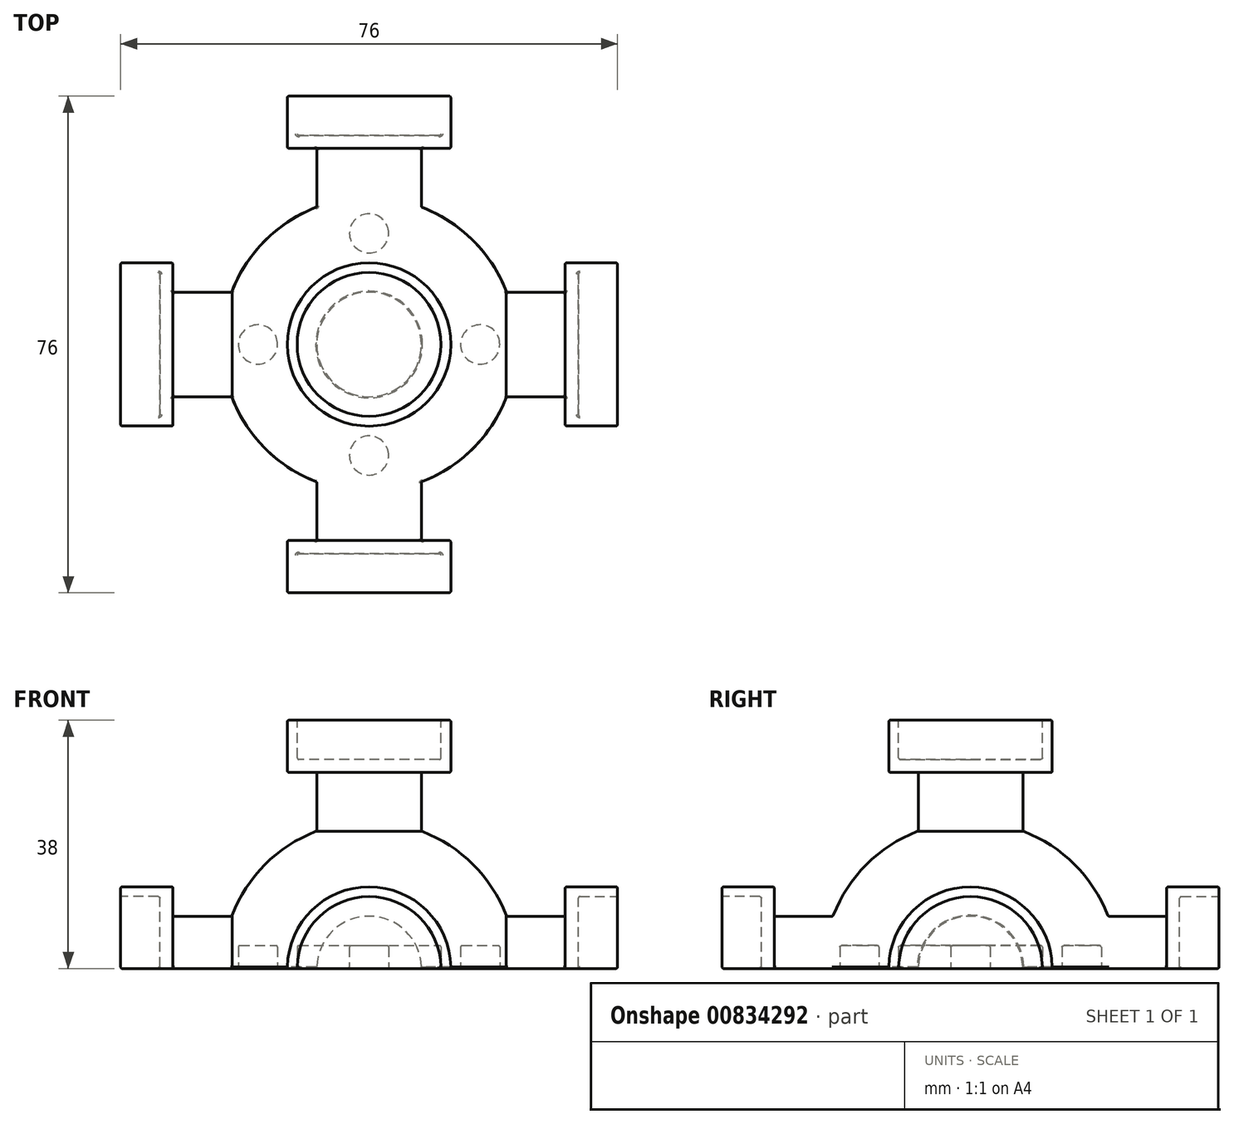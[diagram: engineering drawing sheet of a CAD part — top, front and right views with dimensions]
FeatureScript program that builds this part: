
annotation { "Feature Type Name" : "Feature", "Feature Type Description" : "" }
export const myFeature = defineFeature(function(context is Context, id is Id, definition is map)
    precondition{}
    {
        {
            var Q0;
            Q0=qCreatedBy(makeId("Top.planeOp"),FACE);
            var sketch = newSketch(context, id + "F0", { "sketchPlane" : qUnion([Q0])});
            skCircle(sketch, "E0", {"center": v(0, 0) * mm, "radius": 22.5 * mm});
            skLineSegment(sketch, "E1", {"start": v(0, 22.5) * mm, "end": v(0, -22.5) * mm});
            skSolve(sketch);
        }
        {
            var Q0;
            {var subQ0=sQuery(id+"F0.wireOp",EDGE,"E1");Q0=makeQuery(id+"F0.imprint","IMPRINT",FACE,{"disambiguationData":[TD([[makeQuery(id+"F0.imprint","IMPRINT",EDGE,{"derivedFrom":subQ0}),1.0]])]});}
            var Q1;
            Q1=sQuery(id+"F0.wireOp",EDGE,"E1");
            revolve(context, id + "F1", {"surfaceOperationType" : NewSurfaceOperationType.NEW, "entities" : qUnion([Q0]), "axis" : qUnion([Q1]), "revolveType" : RevolveType.ONE_DIRECTION, "angle" : 180 * degree});
        }
        {
            var Q0;
            Q0=makeQuery(id+"F1.opRevolve","CAP_FACE",FACE,{"disambiguationData":[OSD([sQuery(id+"F0.wireOp",EDGE,"E0"),sQuery(id+"F0.wireOp",EDGE,"E1")])],"isStart":true});
            var sketch = newSketch(context, id + "F2", { "sketchPlane" : qUnion([Q0])});
            skCircle(sketch, "E2", {"center": v(0, 0) * mm, "radius": 11 * mm});
            skCircle(sketch, "E3", {"center": v(0, -17) * mm, "radius": 3 * mm});
            skCircle(sketch, "E4", {"center": v(-17, 0) * mm, "radius": 3 * mm});
            skCircle(sketch, "E5.MirrorC", {"center": v(17, 0) * mm, "radius": 3 * mm});
            skCircle(sketch, "E6.MirrorC", {"center": v(0, 17) * mm, "radius": 3 * mm});
            skSolve(sketch);
        }
        {
            var Q0;
            Q0 = qSketchRegion(id + "F2", true);
            extrude(context, id + "F3", {"entities" : qUnion([Q0]), "operationType" : NewBodyOperationType.REMOVE, "oppositeDirection" : true, "depth" : 3.5 * mm, "offsetDistance" : 25 * mm});
        }
        {
            var Q0;
            Q0=qCreatedBy(makeId("Top.planeOp"),FACE);
            cPlane(context, id + "F4", {"entities" : qUnion([Q0]), "cplaneType" : CPlaneType.OFFSET, "offset" : 20 * mm, "width" : 150 * mm, "height" : 150 * mm});
        }
        {
            var Q0;
            Q0=qCreatedBy(id+"F4.planeOp",FACE);
            var sketch = newSketch(context, id + "F5", { "sketchPlane" : qUnion([Q0])});
            skCircle(sketch, "E7", {"center": v(0, 0) * mm, "radius": 8 * mm});
            skSolve(sketch);
        }
        {
            var Q0;
            Q0 = qSketchRegion(id + "F5", true);
            extrude(context, id + "F6", {"entities" : qUnion([Q0]), "operationType" : NewBodyOperationType.ADD, "depth" : 10 * mm, "offsetDistance" : 25 * mm});
        }
        {
            var Q0;
            Q0=makeQuery(id+"F6.opExtrude","CAP_FACE",FACE,{"disambiguationData":[OSD([sQuery(id+"F5.wireOp",EDGE,"E7")])],"isStart":false});
            var sketch = newSketch(context, id + "F7", { "sketchPlane" : qUnion([Q0])});
            skCircle(sketch, "E8", {"center": v(0, 0) * mm, "radius": 12.5 * mm});
            skSolve(sketch);
        }
        {
            var Q0;
            Q0 = qSketchRegion(id + "F7", true);
            extrude(context, id + "F8", {"entities" : qUnion([Q0]), "operationType" : NewBodyOperationType.ADD, "depth" : 8 * mm, "offsetDistance" : 25 * mm});
        }
        {
            var Q0;
            Q0=makeQuery(id+"F8.opExtrude","CAP_FACE",FACE,{"disambiguationData":[OSD([sQuery(id+"F7.wireOp",EDGE,"E8")])],"isStart":false});
            var sketch = newSketch(context, id + "F9", { "sketchPlane" : qUnion([Q0])});
            skCircle(sketch, "E9", {"center": v(0, 0) * mm, "radius": 11 * mm});
            skSolve(sketch);
        }
        {
            var Q0;
            Q0 = qSketchRegion(id + "F9", true);
            extrude(context, id + "F10", {"entities" : qUnion([Q0]), "operationType" : NewBodyOperationType.REMOVE, "oppositeDirection" : true, "depth" : 6 * mm, "offsetDistance" : 25 * mm});
        }
        {
            var Q0;
            Q0=qCreatedBy(makeId("Front.planeOp"),FACE);
            cPlane(context, id + "F11", {"entities" : qUnion([Q0]), "cplaneType" : CPlaneType.OFFSET, "offset" : 20 * mm, "width" : 150 * mm, "height" : 150 * mm});
        }
        {
            var Q0;
            Q0=qCreatedBy(id+"F11.planeOp",FACE);
            var sketch = newSketch(context, id + "F12", { "sketchPlane" : qUnion([Q0])});
            skArc(sketch, "E10", {"start": v(8, 0) * mm, "mid": v(0, 8) * mm, "end": v(-8, 0) * mm});
            skLineSegment(sketch, "E11", {"start": v(-8, 0) * mm, "end": v(8, 0) * mm});
            skSolve(sketch);
        }
        {
            var Q0;
            Q0 = qSketchRegion(id + "F12", true);
            extrude(context, id + "F13", {"entities" : qUnion([Q0]), "operationType" : NewBodyOperationType.ADD, "depth" : 10 * mm, "offsetDistance" : 25 * mm});
        }
        {
            var Q0;
            Q0=makeQuery(id+"F13.opExtrude","CAP_FACE",FACE,{"disambiguationData":[OSD([sQuery(id+"F12.wireOp",EDGE,"E10"),sQuery(id+"F12.wireOp",EDGE,"E11")])],"isStart":false});
            var sketch = newSketch(context, id + "F14", { "sketchPlane" : qUnion([Q0])});
            skArc(sketch, "E12", {"start": v(12.5, 0) * mm, "mid": v(0, 12.5) * mm, "end": v(-12.5, 0) * mm});
            skLineSegment(sketch, "E13", {"start": v(-12.5, 0) * mm, "end": v(12.5, 0) * mm});
            skSolve(sketch);
        }
        {
            var Q0;
            Q0 = qSketchRegion(id + "F14", true);
            extrude(context, id + "F15", {"entities" : qUnion([Q0]), "operationType" : NewBodyOperationType.ADD, "depth" : 8 * mm, "offsetDistance" : 25 * mm});
        }
        {
            var Q0;
            Q0=makeQuery(id+"F15.opExtrude","CAP_FACE",FACE,{"disambiguationData":[OSD([sQuery(id+"F14.wireOp",EDGE,"E12"),sQuery(id+"F14.wireOp",EDGE,"E13")])],"isStart":false});
            var sketch = newSketch(context, id + "F16", { "sketchPlane" : qUnion([Q0])});
            skArc(sketch, "E14", {"start": v(11, 0) * mm, "mid": v(0, 11) * mm, "end": v(-11, 0) * mm});
            skLineSegment(sketch, "E15", {"start": v(-11, 0) * mm, "end": v(11, 0) * mm});
            skSolve(sketch);
        }
        {
            var Q0;
            Q0 = qSketchRegion(id + "F16", true);
            extrude(context, id + "F17", {"entities" : qUnion([Q0]), "operationType" : NewBodyOperationType.REMOVE, "oppositeDirection" : true, "depth" : 6 * mm, "offsetDistance" : 25 * mm});
        }
        {
            var Q0;
            Q0=qCreatedBy(makeId("Front.planeOp"),FACE);
            cPlane(context, id + "F18", {"entities" : qUnion([Q0]), "cplaneType" : CPlaneType.OFFSET, "offset" : 20 * mm, "oppositeDirection" : true, "width" : 150 * mm, "height" : 150 * mm});
        }
        {
            var Q0;
            Q0=qCreatedBy(id+"F18.planeOp",FACE);
            var sketch = newSketch(context, id + "F19", { "sketchPlane" : qUnion([Q0])});
            skArc(sketch, "E16", {"start": v(8, 0) * mm, "mid": v(0, 8) * mm, "end": v(-8, 0) * mm});
            skLineSegment(sketch, "E17", {"start": v(8, 0) * mm, "end": v(-8, 0) * mm});
            skSolve(sketch);
        }
        {
            var Q0;
            Q0 = qSketchRegion(id + "F19", true);
            extrude(context, id + "F20", {"entities" : qUnion([Q0]), "operationType" : NewBodyOperationType.ADD, "oppositeDirection" : true, "depth" : 10 * mm, "offsetDistance" : 25 * mm});
        }
        {
            var Q0;
            Q0=makeQuery(id+"F20.opExtrude","CAP_FACE",FACE,{"disambiguationData":[OSD([sQuery(id+"F19.wireOp",EDGE,"E16"),sQuery(id+"F19.wireOp",EDGE,"E17")])],"isStart":false});
            var sketch = newSketch(context, id + "F21", { "sketchPlane" : qUnion([Q0])});
            skArc(sketch, "E18", {"start": v(12.5, 0) * mm, "mid": v(0, 12.5) * mm, "end": v(-12.5, 0) * mm});
            skLineSegment(sketch, "E19", {"start": v(-12.5, 0) * mm, "end": v(12.5, 0) * mm});
            skSolve(sketch);
        }
        {
            var Q0;
            Q0 = qSketchRegion(id + "F21", true);
            extrude(context, id + "F22", {"entities" : qUnion([Q0]), "operationType" : NewBodyOperationType.ADD, "depth" : 8 * mm, "offsetDistance" : 25 * mm});
        }
        {
            var Q0;
            Q0=makeQuery(id+"F22.opExtrude","CAP_FACE",FACE,{"disambiguationData":[OSD([sQuery(id+"F21.wireOp",EDGE,"E18"),sQuery(id+"F21.wireOp",EDGE,"E19")])],"isStart":false});
            var sketch = newSketch(context, id + "F23", { "sketchPlane" : qUnion([Q0])});
            skArc(sketch, "E20", {"start": v(11, 0) * mm, "mid": v(0, 11) * mm, "end": v(-11, 0) * mm});
            skLineSegment(sketch, "E21", {"start": v(11, 0) * mm, "end": v(-11, 0) * mm});
            skSolve(sketch);
        }
        {
            var Q0;
            Q0 = qSketchRegion(id + "F23", true);
            extrude(context, id + "F24", {"entities" : qUnion([Q0]), "operationType" : NewBodyOperationType.REMOVE, "oppositeDirection" : true, "depth" : 6 * mm, "offsetDistance" : 25 * mm});
        }
        {
            var Q0;
            Q0=qCreatedBy(makeId("Right.planeOp"),FACE);
            cPlane(context, id + "F25", {"entities" : qUnion([Q0]), "cplaneType" : CPlaneType.OFFSET, "offset" : 20 * mm, "width" : 150 * mm, "height" : 150 * mm});
        }
        {
            var Q0;
            Q0=qCreatedBy(id+"F25.planeOp",FACE);
            var sketch = newSketch(context, id + "F26", { "sketchPlane" : qUnion([Q0])});
            skArc(sketch, "E22", {"start": v(8, 0) * mm, "mid": v(0, 8) * mm, "end": v(-8, 0) * mm});
            skLineSegment(sketch, "E23", {"start": v(-8, 0) * mm, "end": v(8, 0) * mm});
            skSolve(sketch);
        }
        {
            var Q0;
            Q0 = qSketchRegion(id + "F26", true);
            extrude(context, id + "F27", {"entities" : qUnion([Q0]), "operationType" : NewBodyOperationType.ADD, "depth" : 10 * mm, "offsetDistance" : 25 * mm});
        }
        {
            var Q0;
            Q0=makeQuery(id+"F27.opExtrude","CAP_FACE",FACE,{"disambiguationData":[OSD([sQuery(id+"F26.wireOp",EDGE,"E22"),sQuery(id+"F26.wireOp",EDGE,"E23")])],"isStart":false});
            var sketch = newSketch(context, id + "F28", { "sketchPlane" : qUnion([Q0])});
            skArc(sketch, "E24", {"start": v(12.5, 0) * mm, "mid": v(0, 12.5) * mm, "end": v(-12.5, 0) * mm});
            skLineSegment(sketch, "E25", {"start": v(-12.5, 0) * mm, "end": v(12.5, 0) * mm});
            skSolve(sketch);
        }
        {
            var Q0;
            Q0 = qSketchRegion(id + "F28", true);
            extrude(context, id + "F29", {"entities" : qUnion([Q0]), "operationType" : NewBodyOperationType.ADD, "depth" : 8 * mm, "offsetDistance" : 25 * mm});
        }
        {
            var Q0;
            Q0=makeQuery(id+"F29.opExtrude","CAP_FACE",FACE,{"disambiguationData":[OSD([sQuery(id+"F28.wireOp",EDGE,"E24"),sQuery(id+"F28.wireOp",EDGE,"E25")])],"isStart":false});
            var sketch = newSketch(context, id + "F30", { "sketchPlane" : qUnion([Q0])});
            skArc(sketch, "E26", {"start": v(11, 0) * mm, "mid": v(0, 11) * mm, "end": v(-11, 0) * mm});
            skLineSegment(sketch, "E27", {"start": v(-11, 0) * mm, "end": v(11, 0) * mm});
            skSolve(sketch);
        }
        {
            var Q0;
            Q0 = qSketchRegion(id + "F30", true);
            extrude(context, id + "F31", {"entities" : qUnion([Q0]), "operationType" : NewBodyOperationType.REMOVE, "oppositeDirection" : true, "depth" : 6 * mm, "offsetDistance" : 25 * mm});
        }
        {
            var Q0;
            Q0=qCreatedBy(makeId("Right.planeOp"),FACE);
            cPlane(context, id + "F32", {"entities" : qUnion([Q0]), "cplaneType" : CPlaneType.OFFSET, "offset" : 20 * mm, "oppositeDirection" : true, "width" : 150 * mm, "height" : 150 * mm});
        }
        {
            var Q0;
            Q0=qCreatedBy(id+"F32.planeOp",FACE);
            var sketch = newSketch(context, id + "F33", { "sketchPlane" : qUnion([Q0])});
            skArc(sketch, "E28", {"start": v(8, 0) * mm, "mid": v(0, 8) * mm, "end": v(-8, 0) * mm});
            skLineSegment(sketch, "E29", {"start": v(8, 0) * mm, "end": v(-8, 0) * mm});
            skSolve(sketch);
        }
        {
            var Q0;
            Q0 = qSketchRegion(id + "F33", true);
            extrude(context, id + "F34", {"entities" : qUnion([Q0]), "operationType" : NewBodyOperationType.ADD, "oppositeDirection" : true, "depth" : 10 * mm, "offsetDistance" : 25 * mm});
        }
        {
            var Q0;
            Q0=makeQuery(id+"F34.opExtrude","CAP_FACE",FACE,{"disambiguationData":[OSD([sQuery(id+"F33.wireOp",EDGE,"E28"),sQuery(id+"F33.wireOp",EDGE,"E29")])],"isStart":false});
            var sketch = newSketch(context, id + "F35", { "sketchPlane" : qUnion([Q0])});
            skArc(sketch, "E30", {"start": v(12.5, 0) * mm, "mid": v(0, 12.5) * mm, "end": v(-12.5, 0) * mm});
            skLineSegment(sketch, "E31", {"start": v(-12.5, 0) * mm, "end": v(12.5, 0) * mm});
            skSolve(sketch);
        }
        {
            var Q0;
            Q0 = qSketchRegion(id + "F35", true);
            extrude(context, id + "F36", {"entities" : qUnion([Q0]), "operationType" : NewBodyOperationType.ADD, "depth" : 8 * mm, "offsetDistance" : 25 * mm});
        }
        {
            var Q0;
            Q0=makeQuery(id+"F36.opExtrude","CAP_FACE",FACE,{"disambiguationData":[OSD([sQuery(id+"F35.wireOp",EDGE,"E30"),sQuery(id+"F35.wireOp",EDGE,"E31")])],"isStart":false});
            var sketch = newSketch(context, id + "F37", { "sketchPlane" : qUnion([Q0])});
            skArc(sketch, "E32", {"start": v(11, 0) * mm, "mid": v(0, 11) * mm, "end": v(-11, 0) * mm});
            skLineSegment(sketch, "E33", {"start": v(-11, 0) * mm, "end": v(11, 0) * mm});
            skSolve(sketch);
        }
        {
            var Q0;
            Q0 = qSketchRegion(id + "F37", true);
            extrude(context, id + "F38", {"entities" : qUnion([Q0]), "operationType" : NewBodyOperationType.REMOVE, "oppositeDirection" : true, "depth" : 6 * mm, "offsetDistance" : 25 * mm});
        }
        {
            var Q0;
            Q0=makeQuery(id+"F36.opExtrude","SWEPT_FACE",FACE,{"disambiguationData":[OSD([sQuery(id+"F35.wireOp",EDGE,"E30")])]});
            var Q1;
            Q1=makeQuery(id+"F10.boolean.opBoolean","COPY",EDGE,{"derivedFrom":makeQuery(id+"F10.opExtrude","CAP_EDGE",EDGE,{"disambiguationData":[OSD([sQuery(id+"F9.wireOp",EDGE,"E9")])],"isStart":true})});
            var Q2;
            Q2=makeQuery(id+"F8.opExtrude","CAP_EDGE",EDGE,{"disambiguationData":[OSD([sQuery(id+"F7.wireOp",EDGE,"E8")])],"isStart":false});
            var Q3;
            Q3=makeQuery(id+"F13.opExtrude","SWEPT_FACE",FACE,{"disambiguationData":[OSD([sQuery(id+"F12.wireOp",EDGE,"E10")])]});
            var Q4;
            Q4=makeQuery(id+"F15.opExtrude","SWEPT_FACE",FACE,{"disambiguationData":[OSD([sQuery(id+"F14.wireOp",EDGE,"E12")])]});
            var Q5;
            Q5=makeQuery(id+"F15.opExtrude","CAP_FACE",FACE,{"disambiguationData":[OSD([sQuery(id+"F14.wireOp",EDGE,"E12"),sQuery(id+"F14.wireOp",EDGE,"E13")])],"isStart":true});
            var Q6;
            Q6=makeQuery(id+"F10.boolean.opBoolean","COPY",FACE,{"derivedFrom":makeQuery(id+"F10.opExtrude","SWEPT_FACE",FACE,{"disambiguationData":[OSD([sQuery(id+"F9.wireOp",EDGE,"E9")])]})});
            var Q7;
            Q7=makeQuery(id+"F8.opExtrude","SWEPT_FACE",FACE,{"disambiguationData":[OSD([sQuery(id+"F7.wireOp",EDGE,"E8")])]});
            var Q8;
            Q8=makeQuery(id+"F8.opExtrude","CAP_FACE",FACE,{"disambiguationData":[OSD([sQuery(id+"F7.wireOp",EDGE,"E8")])],"isStart":false});
            var Q9;
            Q9=makeQuery(id+"F15.opExtrude","CAP_FACE",FACE,{"disambiguationData":[OSD([sQuery(id+"F14.wireOp",EDGE,"E12"),sQuery(id+"F14.wireOp",EDGE,"E13")])],"isStart":false});
            var Q10;
            Q10=makeQuery(id+"F10.boolean.opBoolean","COPY",FACE,{"derivedFrom":makeQuery(id+"F10.opExtrude","CAP_FACE",FACE,{"disambiguationData":[OSD([sQuery(id+"F9.wireOp",EDGE,"E9")])],"isStart":false})});
            var Q11;
            Q11=makeQuery(id+"F22.opExtrude","SWEPT_FACE",FACE,{"disambiguationData":[OSD([sQuery(id+"F21.wireOp",EDGE,"E18")])]});
            var Q12;
            Q12=makeQuery(id+"F20.opExtrude","SWEPT_FACE",FACE,{"disambiguationData":[OSD([sQuery(id+"F19.wireOp",EDGE,"E16")])]});
            var Q13;
            Q13=makeQuery(id+"F22.opExtrude","CAP_FACE",FACE,{"disambiguationData":[OSD([sQuery(id+"F21.wireOp",EDGE,"E18"),sQuery(id+"F21.wireOp",EDGE,"E19")])],"isStart":false});
            var Q14;
            Q14=makeQuery(id+"F29.opExtrude","SWEPT_FACE",FACE,{"disambiguationData":[OSD([sQuery(id+"F28.wireOp",EDGE,"E24")])]});
            var Q15;
            Q15=makeQuery(id+"F27.opExtrude","SWEPT_FACE",FACE,{"disambiguationData":[OSD([sQuery(id+"F26.wireOp",EDGE,"E22")])]});
            var Q16;
            Q16=makeQuery(id+"F29.opExtrude","CAP_FACE",FACE,{"disambiguationData":[OSD([sQuery(id+"F28.wireOp",EDGE,"E24"),sQuery(id+"F28.wireOp",EDGE,"E25")])],"isStart":false});
            var Q17;
            Q17=makeQuery(id+"F1.opRevolve","SWEPT_FACE",FACE,{"disambiguationData":[OSD([sQuery(id+"F0.wireOp",EDGE,"E0")])]});
            var Q18;
            Q18=makeQuery(id+"F34.opExtrude","SWEPT_FACE",FACE,{"disambiguationData":[OSD([sQuery(id+"F33.wireOp",EDGE,"E28")])]});
            var Q19;
            Q19=makeQuery(id+"F36.opExtrude","CAP_FACE",FACE,{"disambiguationData":[OSD([sQuery(id+"F35.wireOp",EDGE,"E30"),sQuery(id+"F35.wireOp",EDGE,"E31")])],"isStart":false});
            var Q20;
            Q20=makeQuery(id+"F36.boolean.opBoolean","MERGE",FACE,{"derivedFrom":[makeQuery(id+"F34.boolean.opBoolean","MERGE",FACE,{"derivedFrom":[makeQuery(id+"F29.boolean.opBoolean","MERGE",FACE,{"derivedFrom":[makeQuery(id+"F27.boolean.opBoolean","MERGE",FACE,{"derivedFrom":[makeQuery(id+"F22.boolean.opBoolean","MERGE",FACE,{"derivedFrom":[makeQuery(id+"F20.boolean.opBoolean","MERGE",FACE,{"derivedFrom":[makeQuery(id+"F15.boolean.opBoolean","MERGE",FACE,{"derivedFrom":[makeQuery(id+"F13.boolean.opBoolean","MERGE",FACE,{"derivedFrom":[makeQuery(id+"F1.opRevolve","CAP_FACE",FACE,{"disambiguationData":[OSD([sQuery(id+"F0.wireOp",EDGE,"E0"),sQuery(id+"F0.wireOp",EDGE,"E1")])],"isStart":true}),makeQuery(id+"F13.opExtrude","SWEPT_FACE",FACE,{"disambiguationData":[OSD([sQuery(id+"F12.wireOp",EDGE,"E11")])]})]}),makeQuery(id+"F15.opExtrude","SWEPT_FACE",FACE,{"disambiguationData":[OSD([sQuery(id+"F14.wireOp",EDGE,"E13")])]})]}),makeQuery(id+"F20.opExtrude","SWEPT_FACE",FACE,{"disambiguationData":[OSD([sQuery(id+"F19.wireOp",EDGE,"E17")])]})]}),makeQuery(id+"F22.opExtrude","SWEPT_FACE",FACE,{"disambiguationData":[OSD([sQuery(id+"F21.wireOp",EDGE,"E19")])]})]}),makeQuery(id+"F27.opExtrude","SWEPT_FACE",FACE,{"disambiguationData":[OSD([sQuery(id+"F26.wireOp",EDGE,"E23")])]})]}),makeQuery(id+"F29.opExtrude","SWEPT_FACE",FACE,{"disambiguationData":[OSD([sQuery(id+"F28.wireOp",EDGE,"E25")])]})]}),makeQuery(id+"F34.opExtrude","SWEPT_FACE",FACE,{"disambiguationData":[OSD([sQuery(id+"F33.wireOp",EDGE,"E29")])]})]}),makeQuery(id+"F36.opExtrude","SWEPT_FACE",FACE,{"disambiguationData":[OSD([sQuery(id+"F35.wireOp",EDGE,"E31")])]})]});
            var Q21;
            Q21=makeQuery(id+"F3.boolean.opBoolean","COPY",FACE,{"derivedFrom":makeQuery(id+"F3.opExtrude","SWEPT_FACE",FACE,{"disambiguationData":[OSD([sQuery(id+"F2.wireOp",EDGE,"E6.MirrorC")])]})});
            var Q22;
            Q22=makeQuery(id+"F3.boolean.opBoolean","COPY",FACE,{"derivedFrom":makeQuery(id+"F3.opExtrude","CAP_FACE",FACE,{"disambiguationData":[OSD([sQuery(id+"F2.wireOp",EDGE,"E5.MirrorC")])],"isStart":false})});
            var Q23;
            Q23=makeQuery(id+"F3.boolean.opBoolean","COPY",FACE,{"derivedFrom":makeQuery(id+"F3.opExtrude","SWEPT_FACE",FACE,{"disambiguationData":[OSD([sQuery(id+"F2.wireOp",EDGE,"E5.MirrorC")])]})});
            var Q24;
            Q24=makeQuery(id+"F3.boolean.opBoolean","COPY",FACE,{"derivedFrom":makeQuery(id+"F3.opExtrude","SWEPT_FACE",FACE,{"disambiguationData":[OSD([sQuery(id+"F2.wireOp",EDGE,"E3")])]})});
            var Q25;
            {var subQ0=sQuery(id+"F21.wireOp",EDGE,"E19");var subQ1=sQuery(id+"F21.wireOp",EDGE,"E18");Q25=makeQuery(id+"F22.opExtrude","SWEPT_EDGE",EDGE,{"disambiguationData":[OSD([subQ1,subQ0]),TDD([makeQuery(id+"F21.imprint","INTERSECT",VERTEX,{"disambiguationData":[OD(0.0)],"derivedFrom":[subQ1,subQ0]})])]});}
            var Q26;
            Q26=makeQuery(id+"F3.boolean.opBoolean","COPY",FACE,{"derivedFrom":makeQuery(id+"F3.opExtrude","CAP_FACE",FACE,{"disambiguationData":[OSD([sQuery(id+"F2.wireOp",EDGE,"E4")])],"isStart":false})});
            var Q27;
            {var subQ0=sQuery(id+"F35.wireOp",EDGE,"E31");var subQ1=sQuery(id+"F35.wireOp",EDGE,"E30");Q27=makeQuery(id+"F36.opExtrude","SWEPT_EDGE",EDGE,{"disambiguationData":[OSD([subQ1,subQ0]),TDD([makeQuery(id+"F35.imprint","INTERSECT",VERTEX,{"disambiguationData":[OD(0.0)],"derivedFrom":[subQ1,subQ0]})])]});}
            var Q28;
            Q28=makeQuery(id+"F20.boolean.opBoolean","INTERSECT",EDGE,{"derivedFrom":[makeQuery(id+"F1.opRevolve","SWEPT_FACE",FACE,{"disambiguationData":[OSD([sQuery(id+"F0.wireOp",EDGE,"E0")])]}),makeQuery(id+"F20.opExtrude","SWEPT_FACE",FACE,{"disambiguationData":[OSD([sQuery(id+"F19.wireOp",EDGE,"E16")])]})]});
            var Q29;
            Q29=makeQuery(id+"F6.opExtrude","SWEPT_FACE",FACE,{"disambiguationData":[OSD([sQuery(id+"F5.wireOp",EDGE,"E7")])]});
            var Q30;
            Q30=makeQuery(id+"F3.boolean.opBoolean","COPY",FACE,{"derivedFrom":makeQuery(id+"F3.opExtrude","CAP_FACE",FACE,{"disambiguationData":[OSD([sQuery(id+"F2.wireOp",EDGE,"E6.MirrorC")])],"isStart":false})});
            var Q31;
            Q31=makeQuery(id+"F8.opExtrude","CAP_EDGE",EDGE,{"disambiguationData":[OSD([sQuery(id+"F7.wireOp",EDGE,"E8")])],"isStart":true});
            var Q32;
            Q32=makeQuery(id+"F13.boolean.opBoolean","INTERSECT",EDGE,{"derivedFrom":[makeQuery(id+"F1.opRevolve","SWEPT_FACE",FACE,{"disambiguationData":[OSD([sQuery(id+"F0.wireOp",EDGE,"E0")])]}),makeQuery(id+"F13.opExtrude","SWEPT_FACE",FACE,{"disambiguationData":[OSD([sQuery(id+"F12.wireOp",EDGE,"E10")])]})]});
            var Q33;
            {var subQ0=sQuery(id+"F12.wireOp",EDGE,"E11");var subQ1=sQuery(id+"F12.wireOp",EDGE,"E10");Q33=makeQuery(id+"F13.opExtrude","SWEPT_EDGE",EDGE,{"disambiguationData":[OSD([subQ1,subQ0]),TDD([makeQuery(id+"F12.imprint","INTERSECT",VERTEX,{"disambiguationData":[OD(1.0)],"derivedFrom":[subQ1,subQ0]})])]});}
            var Q34;
            {var subQ0=sQuery(id+"F14.wireOp",EDGE,"E13");var subQ1=sQuery(id+"F14.wireOp",EDGE,"E12");Q34=makeQuery(id+"F15.opExtrude","SWEPT_EDGE",EDGE,{"disambiguationData":[OSD([subQ1,subQ0]),TDD([makeQuery(id+"F14.imprint","INTERSECT",VERTEX,{"disambiguationData":[OD(1.0)],"derivedFrom":[subQ1,subQ0]})])]});}
            var Q35;
            {var subQ0=sQuery(id+"F14.wireOp",EDGE,"E13");var subQ1=sQuery(id+"F14.wireOp",EDGE,"E12");Q35=makeQuery(id+"F15.opExtrude","SWEPT_EDGE",EDGE,{"disambiguationData":[OSD([subQ1,subQ0]),TDD([makeQuery(id+"F14.imprint","INTERSECT",VERTEX,{"disambiguationData":[OD(0.0)],"derivedFrom":[subQ1,subQ0]})])]});}
            var Q36;
            Q36=makeQuery(id+"F17.boolean.opBoolean","COPY",FACE,{"derivedFrom":makeQuery(id+"F17.opExtrude","CAP_FACE",FACE,{"disambiguationData":[OSD([sQuery(id+"F16.wireOp",EDGE,"E14"),sQuery(id+"F16.wireOp",EDGE,"E15")])],"isStart":false})});
            var Q37;
            Q37=makeQuery(id+"F17.boolean.opBoolean","COPY",FACE,{"derivedFrom":makeQuery(id+"F17.opExtrude","SWEPT_FACE",FACE,{"disambiguationData":[OSD([sQuery(id+"F16.wireOp",EDGE,"E14")])]})});
            var Q38;
            Q38=makeQuery(id+"F10.boolean.opBoolean","COPY",EDGE,{"derivedFrom":makeQuery(id+"F10.opExtrude","CAP_EDGE",EDGE,{"disambiguationData":[OSD([sQuery(id+"F9.wireOp",EDGE,"E9")])],"isStart":false})});
            var Q39;
            Q39=makeQuery(id+"F6.opExtrude","CAP_EDGE",EDGE,{"disambiguationData":[OSD([sQuery(id+"F5.wireOp",EDGE,"E7")])],"isStart":false});
            var Q40;
            {var subQ0=sQuery(id+"F21.wireOp",EDGE,"E19");var subQ1=sQuery(id+"F21.wireOp",EDGE,"E18");Q40=makeQuery(id+"F22.opExtrude","SWEPT_EDGE",EDGE,{"disambiguationData":[OSD([subQ1,subQ0]),TDD([makeQuery(id+"F21.imprint","INTERSECT",VERTEX,{"disambiguationData":[OD(1.0)],"derivedFrom":[subQ1,subQ0]})])]});}
            var Q41;
            Q41=makeQuery(id+"F8.opExtrude","CAP_FACE",FACE,{"disambiguationData":[OSD([sQuery(id+"F7.wireOp",EDGE,"E8")])],"isStart":true});
            var Q42;
            Q42=makeQuery(id+"F15.opExtrude","CAP_EDGE",EDGE,{"disambiguationData":[OSD([sQuery(id+"F14.wireOp",EDGE,"E12")])],"isStart":true});
            var Q43;
            Q43=makeQuery(id+"F15.opExtrude","CAP_EDGE",EDGE,{"disambiguationData":[OSD([sQuery(id+"F14.wireOp",EDGE,"E12")])],"isStart":false});
            var Q44;
            {var subQ0=sQuery(id+"F12.wireOp",EDGE,"E11");var subQ1=sQuery(id+"F12.wireOp",EDGE,"E10");Q44=makeQuery(id+"F13.opExtrude","SWEPT_EDGE",EDGE,{"disambiguationData":[OSD([subQ1,subQ0]),TDD([makeQuery(id+"F12.imprint","INTERSECT",VERTEX,{"disambiguationData":[OD(0.0)],"derivedFrom":[subQ1,subQ0]})])]});}
            var Q45;
            Q45=makeQuery(id+"F3.boolean.opBoolean","COPY",FACE,{"derivedFrom":makeQuery(id+"F3.opExtrude","CAP_FACE",FACE,{"disambiguationData":[OSD([sQuery(id+"F2.wireOp",EDGE,"E3")])],"isStart":false})});
            var Q46;
            {var subQ0=sQuery(id+"F19.wireOp",EDGE,"E17");var subQ1=sQuery(id+"F19.wireOp",EDGE,"E16");Q46=makeQuery(id+"F20.opExtrude","SWEPT_EDGE",EDGE,{"disambiguationData":[OSD([subQ1,subQ0]),TDD([makeQuery(id+"F19.imprint","INTERSECT",VERTEX,{"disambiguationData":[OD(0.0)],"derivedFrom":[subQ1,subQ0]})])]});}
            var Q47;
            {var subQ0=sQuery(id+"F19.wireOp",EDGE,"E17");var subQ1=sQuery(id+"F19.wireOp",EDGE,"E16");Q47=makeQuery(id+"F20.opExtrude","SWEPT_EDGE",EDGE,{"disambiguationData":[OSD([subQ1,subQ0]),TDD([makeQuery(id+"F19.imprint","INTERSECT",VERTEX,{"disambiguationData":[OD(1.0)],"derivedFrom":[subQ1,subQ0]})])]});}
            var Q48;
            Q48=makeQuery(id+"F24.boolean.opBoolean","COPY",FACE,{"derivedFrom":makeQuery(id+"F24.opExtrude","SWEPT_FACE",FACE,{"disambiguationData":[OSD([sQuery(id+"F23.wireOp",EDGE,"E20")])]})});
            var Q49;
            Q49=makeQuery(id+"F22.opExtrude","CAP_EDGE",EDGE,{"disambiguationData":[OSD([sQuery(id+"F21.wireOp",EDGE,"E18")])],"isStart":false});
            var Q50;
            Q50=makeQuery(id+"F22.opExtrude","CAP_FACE",FACE,{"disambiguationData":[OSD([sQuery(id+"F21.wireOp",EDGE,"E18"),sQuery(id+"F21.wireOp",EDGE,"E19")])],"isStart":true});
            var Q51;
            Q51=makeQuery(id+"F24.boolean.opBoolean","COPY",FACE,{"derivedFrom":makeQuery(id+"F24.opExtrude","CAP_FACE",FACE,{"disambiguationData":[OSD([sQuery(id+"F23.wireOp",EDGE,"E20"),sQuery(id+"F23.wireOp",EDGE,"E21")])],"isStart":false})});
            var Q52;
            {var subQ0=sQuery(id+"F28.wireOp",EDGE,"E25");var subQ1=sQuery(id+"F28.wireOp",EDGE,"E24");Q52=makeQuery(id+"F29.opExtrude","SWEPT_EDGE",EDGE,{"disambiguationData":[OSD([subQ1,subQ0]),TDD([makeQuery(id+"F28.imprint","INTERSECT",VERTEX,{"disambiguationData":[OD(1.0)],"derivedFrom":[subQ1,subQ0]})])]});}
            var Q53;
            {var subQ0=sQuery(id+"F28.wireOp",EDGE,"E25");var subQ1=sQuery(id+"F28.wireOp",EDGE,"E24");Q53=makeQuery(id+"F29.opExtrude","SWEPT_EDGE",EDGE,{"disambiguationData":[OSD([subQ1,subQ0]),TDD([makeQuery(id+"F28.imprint","INTERSECT",VERTEX,{"disambiguationData":[OD(0.0)],"derivedFrom":[subQ1,subQ0]})])]});}
            var Q54;
            Q54=makeQuery(id+"F27.boolean.opBoolean","INTERSECT",EDGE,{"derivedFrom":[makeQuery(id+"F1.opRevolve","SWEPT_FACE",FACE,{"disambiguationData":[OSD([sQuery(id+"F0.wireOp",EDGE,"E0")])]}),makeQuery(id+"F27.opExtrude","SWEPT_FACE",FACE,{"disambiguationData":[OSD([sQuery(id+"F26.wireOp",EDGE,"E22")])]})]});
            var Q55;
            {var subQ0=sQuery(id+"F26.wireOp",EDGE,"E23");var subQ1=sQuery(id+"F26.wireOp",EDGE,"E22");Q55=makeQuery(id+"F27.opExtrude","SWEPT_EDGE",EDGE,{"disambiguationData":[OSD([subQ1,subQ0]),TDD([makeQuery(id+"F26.imprint","INTERSECT",VERTEX,{"disambiguationData":[OD(0.0)],"derivedFrom":[subQ1,subQ0]})])]});}
            var Q56;
            {var subQ0=sQuery(id+"F26.wireOp",EDGE,"E23");var subQ1=sQuery(id+"F26.wireOp",EDGE,"E22");Q56=makeQuery(id+"F27.opExtrude","SWEPT_EDGE",EDGE,{"disambiguationData":[OSD([subQ1,subQ0]),TDD([makeQuery(id+"F26.imprint","INTERSECT",VERTEX,{"disambiguationData":[OD(1.0)],"derivedFrom":[subQ1,subQ0]})])]});}
            var Q57;
            {var subQ0=sQuery(id+"F0.wireOp",EDGE,"E0");Q57=makeQuery(id+"F27.boolean.opBoolean","SPLIT",EDGE,{"disambiguationData":[TD([makeQuery(id+"F13.opExtrude","SWEPT_FACE",FACE,{"disambiguationData":[OSD([sQuery(id+"F12.wireOp",EDGE,"E10")])]})])],"derivedFrom":makeQuery(id+"F20.boolean.opBoolean","SPLIT",EDGE,{"disambiguationData":[OD(0.0)],"derivedFrom":makeQuery(id+"F1.opRevolve","CAP_EDGE",EDGE,{"disambiguationData":[OSD([subQ0])],"isStart":true})})});}
            var Q58;
            {var subQ0=sQuery(id+"F0.wireOp",EDGE,"E0");Q58=makeQuery(id+"F27.boolean.opBoolean","SPLIT",EDGE,{"disambiguationData":[TD([makeQuery(id+"F20.opExtrude","SWEPT_FACE",FACE,{"disambiguationData":[OSD([sQuery(id+"F19.wireOp",EDGE,"E16")])]})])],"derivedFrom":makeQuery(id+"F20.boolean.opBoolean","SPLIT",EDGE,{"disambiguationData":[OD(0.0)],"derivedFrom":makeQuery(id+"F1.opRevolve","CAP_EDGE",EDGE,{"disambiguationData":[OSD([subQ0])],"isStart":true})})});}
            var Q59;
            Q59=makeQuery(id+"F31.boolean.opBoolean","COPY",FACE,{"derivedFrom":makeQuery(id+"F31.opExtrude","SWEPT_FACE",FACE,{"disambiguationData":[OSD([sQuery(id+"F30.wireOp",EDGE,"E26")])]})});
            var Q60;
            Q60=makeQuery(id+"F29.opExtrude","CAP_EDGE",EDGE,{"disambiguationData":[OSD([sQuery(id+"F28.wireOp",EDGE,"E24")])],"isStart":false});
            var Q61;
            Q61=makeQuery(id+"F29.opExtrude","CAP_FACE",FACE,{"disambiguationData":[OSD([sQuery(id+"F28.wireOp",EDGE,"E24"),sQuery(id+"F28.wireOp",EDGE,"E25")])],"isStart":true});
            var Q62;
            Q62=makeQuery(id+"F31.boolean.opBoolean","COPY",FACE,{"derivedFrom":makeQuery(id+"F31.opExtrude","CAP_FACE",FACE,{"disambiguationData":[OSD([sQuery(id+"F30.wireOp",EDGE,"E26"),sQuery(id+"F30.wireOp",EDGE,"E27")])],"isStart":false})});
            var Q63;
            Q63=makeQuery(id+"F3.boolean.opBoolean","COPY",FACE,{"derivedFrom":makeQuery(id+"F3.opExtrude","SWEPT_FACE",FACE,{"disambiguationData":[OSD([sQuery(id+"F2.wireOp",EDGE,"E4")])]})});
            var Q64;
            Q64=makeQuery(id+"F3.boolean.opBoolean","COPY",FACE,{"derivedFrom":makeQuery(id+"F3.opExtrude","CAP_FACE",FACE,{"disambiguationData":[OSD([sQuery(id+"F2.wireOp",EDGE,"E2")])],"isStart":false})});
            var Q65;
            Q65=makeQuery(id+"F34.boolean.opBoolean","INTERSECT",EDGE,{"derivedFrom":[makeQuery(id+"F1.opRevolve","SWEPT_FACE",FACE,{"disambiguationData":[OSD([sQuery(id+"F0.wireOp",EDGE,"E0")])]}),makeQuery(id+"F34.opExtrude","SWEPT_FACE",FACE,{"disambiguationData":[OSD([sQuery(id+"F33.wireOp",EDGE,"E28")])]})]});
            var Q66;
            {var subQ0=sQuery(id+"F35.wireOp",EDGE,"E31");var subQ1=sQuery(id+"F35.wireOp",EDGE,"E30");Q66=makeQuery(id+"F36.opExtrude","SWEPT_EDGE",EDGE,{"disambiguationData":[OSD([subQ1,subQ0]),TDD([makeQuery(id+"F35.imprint","INTERSECT",VERTEX,{"disambiguationData":[OD(1.0)],"derivedFrom":[subQ1,subQ0]})])]});}
            var Q67;
            {var subQ0=sQuery(id+"F33.wireOp",EDGE,"E29");var subQ1=sQuery(id+"F33.wireOp",EDGE,"E28");Q67=makeQuery(id+"F34.opExtrude","SWEPT_EDGE",EDGE,{"disambiguationData":[OSD([subQ1,subQ0]),TDD([makeQuery(id+"F33.imprint","INTERSECT",VERTEX,{"disambiguationData":[OD(0.0)],"derivedFrom":[subQ1,subQ0]})])]});}
            var Q68;
            {var subQ0=sQuery(id+"F33.wireOp",EDGE,"E29");var subQ1=sQuery(id+"F33.wireOp",EDGE,"E28");Q68=makeQuery(id+"F34.opExtrude","SWEPT_EDGE",EDGE,{"disambiguationData":[OSD([subQ1,subQ0]),TDD([makeQuery(id+"F33.imprint","INTERSECT",VERTEX,{"disambiguationData":[OD(1.0)],"derivedFrom":[subQ1,subQ0]})])]});}
            var Q69;
            {var subQ0=sQuery(id+"F0.wireOp",EDGE,"E0");Q69=makeQuery(id+"F34.boolean.opBoolean","SPLIT",EDGE,{"disambiguationData":[TD([makeQuery(id+"F13.opExtrude","SWEPT_FACE",FACE,{"disambiguationData":[OSD([sQuery(id+"F12.wireOp",EDGE,"E10")])]})])],"derivedFrom":makeQuery(id+"F20.boolean.opBoolean","SPLIT",EDGE,{"disambiguationData":[OD(1.0)],"derivedFrom":makeQuery(id+"F1.opRevolve","CAP_EDGE",EDGE,{"disambiguationData":[OSD([subQ0])],"isStart":true})})});}
            var Q70;
            {var subQ0=sQuery(id+"F0.wireOp",EDGE,"E0");Q70=makeQuery(id+"F34.boolean.opBoolean","SPLIT",EDGE,{"disambiguationData":[TD([makeQuery(id+"F20.opExtrude","SWEPT_FACE",FACE,{"disambiguationData":[OSD([sQuery(id+"F19.wireOp",EDGE,"E16")])]})])],"derivedFrom":makeQuery(id+"F20.boolean.opBoolean","SPLIT",EDGE,{"disambiguationData":[OD(1.0)],"derivedFrom":makeQuery(id+"F1.opRevolve","CAP_EDGE",EDGE,{"disambiguationData":[OSD([subQ0])],"isStart":true})})});}
            var Q71;
            Q71=makeQuery(id+"F36.opExtrude","CAP_EDGE",EDGE,{"disambiguationData":[OSD([sQuery(id+"F35.wireOp",EDGE,"E30")])],"isStart":false});
            var Q72;
            Q72=makeQuery(id+"F38.boolean.opBoolean","COPY",FACE,{"derivedFrom":makeQuery(id+"F38.opExtrude","SWEPT_FACE",FACE,{"disambiguationData":[OSD([sQuery(id+"F37.wireOp",EDGE,"E32")])]})});
            var Q73;
            Q73=makeQuery(id+"F36.opExtrude","CAP_FACE",FACE,{"disambiguationData":[OSD([sQuery(id+"F35.wireOp",EDGE,"E30"),sQuery(id+"F35.wireOp",EDGE,"E31")])],"isStart":true});
            var Q74;
            Q74=makeQuery(id+"F38.boolean.opBoolean","COPY",FACE,{"derivedFrom":makeQuery(id+"F38.opExtrude","CAP_FACE",FACE,{"disambiguationData":[OSD([sQuery(id+"F37.wireOp",EDGE,"E32"),sQuery(id+"F37.wireOp",EDGE,"E33")])],"isStart":false})});
            var Q75;
            Q75=makeQuery(id+"F3.boolean.opBoolean","COPY",EDGE,{"derivedFrom":makeQuery(id+"F3.opExtrude","CAP_EDGE",EDGE,{"disambiguationData":[OSD([sQuery(id+"F2.wireOp",EDGE,"E2")])],"isStart":false})});
            var Q76;
            Q76=makeQuery(id+"F3.boolean.opBoolean","COPY",EDGE,{"derivedFrom":makeQuery(id+"F3.opExtrude","CAP_EDGE",EDGE,{"disambiguationData":[OSD([sQuery(id+"F2.wireOp",EDGE,"E5.MirrorC")])],"isStart":false})});
            var Q77;
            Q77=makeQuery(id+"F17.boolean.opBoolean","SPLIT",EDGE,{"disambiguationData":[OD(0.0)],"derivedFrom":makeQuery(id+"F15.opExtrude","CAP_EDGE",EDGE,{"disambiguationData":[OSD([sQuery(id+"F14.wireOp",EDGE,"E13")])],"isStart":false})});
            var Q78;
            Q78=makeQuery(id+"F3.boolean.opBoolean","COPY",EDGE,{"derivedFrom":makeQuery(id+"F3.opExtrude","CAP_EDGE",EDGE,{"disambiguationData":[OSD([sQuery(id+"F2.wireOp",EDGE,"E6.MirrorC")])],"isStart":false})});
            var Q79;
            Q79=makeQuery(id+"F3.boolean.opBoolean","COPY",EDGE,{"derivedFrom":makeQuery(id+"F3.opExtrude","CAP_EDGE",EDGE,{"disambiguationData":[OSD([sQuery(id+"F2.wireOp",EDGE,"E4")])],"isStart":false})});
            var Q80;
            {var subQ0=sQuery(id+"F16.wireOp",EDGE,"E15");var subQ1=sQuery(id+"F16.wireOp",EDGE,"E14");var subQ2=sQuery(id+"F14.wireOp",EDGE,"E13");Q80=makeQuery(id+"F17.boolean.opBoolean","COPY",EDGE,{"derivedFrom":makeQuery(id+"F17.opExtrude","SWEPT_EDGE",EDGE,{"disambiguationData":[OSD([subQ2,subQ1,subQ0]),TDD([makeQuery(id+"F16.imprint","INTERSECT",VERTEX,{"disambiguationData":[OD(1.0)],"derivedFrom":[makeQuery(id+"F15.opExtrude","CAP_EDGE",EDGE,{"disambiguationData":[OSD([subQ2])],"isStart":false}),subQ1,subQ0]})])]})});}
            var Q81;
            Q81=makeQuery(id+"F6.boolean.opBoolean","INTERSECT",EDGE,{"derivedFrom":[makeQuery(id+"F1.opRevolve","SWEPT_FACE",FACE,{"disambiguationData":[OSD([sQuery(id+"F0.wireOp",EDGE,"E0")])]}),makeQuery(id+"F6.opExtrude","SWEPT_FACE",FACE,{"disambiguationData":[OSD([sQuery(id+"F5.wireOp",EDGE,"E7")])]})]});
            var Q82;
            Q82=makeQuery(id+"F17.boolean.opBoolean","COPY",EDGE,{"derivedFrom":makeQuery(id+"F17.opExtrude","CAP_EDGE",EDGE,{"disambiguationData":[OSD([sQuery(id+"F16.wireOp",EDGE,"E14")])],"isStart":true})});
            var Q83;
            Q83=makeQuery(id+"F15.boolean.opBoolean","SPLIT",EDGE,{"disambiguationData":[OD(0.0)],"derivedFrom":makeQuery(id+"F15.opExtrude","CAP_EDGE",EDGE,{"disambiguationData":[OSD([sQuery(id+"F14.wireOp",EDGE,"E13")])],"isStart":true})});
            var Q84;
            Q84=makeQuery(id+"F17.boolean.opBoolean","SPLIT",EDGE,{"disambiguationData":[OD(1.0)],"derivedFrom":makeQuery(id+"F15.opExtrude","CAP_EDGE",EDGE,{"disambiguationData":[OSD([sQuery(id+"F14.wireOp",EDGE,"E13")])],"isStart":false})});
            var Q85;
            {var subQ0=sQuery(id+"F16.wireOp",EDGE,"E15");var subQ1=sQuery(id+"F16.wireOp",EDGE,"E14");var subQ2=sQuery(id+"F14.wireOp",EDGE,"E13");Q85=makeQuery(id+"F17.boolean.opBoolean","COPY",EDGE,{"derivedFrom":makeQuery(id+"F17.opExtrude","SWEPT_EDGE",EDGE,{"disambiguationData":[OSD([subQ2,subQ1,subQ0]),TDD([makeQuery(id+"F16.imprint","INTERSECT",VERTEX,{"disambiguationData":[OD(0.0)],"derivedFrom":[makeQuery(id+"F15.opExtrude","CAP_EDGE",EDGE,{"disambiguationData":[OSD([subQ2])],"isStart":false}),subQ1,subQ0]})])]})});}
            var Q86;
            Q86=makeQuery(id+"F13.opExtrude","CAP_EDGE",EDGE,{"disambiguationData":[OSD([sQuery(id+"F12.wireOp",EDGE,"E10")])],"isStart":false});
            var Q87;
            Q87=makeQuery(id+"F15.boolean.opBoolean","SPLIT",EDGE,{"disambiguationData":[OD(1.0)],"derivedFrom":makeQuery(id+"F15.opExtrude","CAP_EDGE",EDGE,{"disambiguationData":[OSD([sQuery(id+"F14.wireOp",EDGE,"E13")])],"isStart":true})});
            var Q88;
            Q88=makeQuery(id+"F17.boolean.opBoolean","COPY",EDGE,{"derivedFrom":makeQuery(id+"F17.opExtrude","CAP_EDGE",EDGE,{"disambiguationData":[OSD([sQuery(id+"F16.wireOp",EDGE,"E14")])],"isStart":false})});
            var Q89;
            Q89=makeQuery(id+"F3.boolean.opBoolean","COPY",EDGE,{"derivedFrom":makeQuery(id+"F3.opExtrude","CAP_EDGE",EDGE,{"disambiguationData":[OSD([sQuery(id+"F2.wireOp",EDGE,"E3")])],"isStart":false})});
            var Q90;
            Q90=makeQuery(id+"F22.opExtrude","CAP_EDGE",EDGE,{"disambiguationData":[OSD([sQuery(id+"F21.wireOp",EDGE,"E18")])],"isStart":true});
            var Q91;
            {var subQ0=sQuery(id+"F23.wireOp",EDGE,"E21");var subQ1=sQuery(id+"F23.wireOp",EDGE,"E20");var subQ2=sQuery(id+"F21.wireOp",EDGE,"E19");Q91=makeQuery(id+"F24.boolean.opBoolean","COPY",EDGE,{"derivedFrom":makeQuery(id+"F24.opExtrude","SWEPT_EDGE",EDGE,{"disambiguationData":[OSD([subQ2,subQ1,subQ0]),TDD([makeQuery(id+"F23.imprint","INTERSECT",VERTEX,{"disambiguationData":[OD(0.0)],"derivedFrom":[makeQuery(id+"F22.opExtrude","CAP_EDGE",EDGE,{"disambiguationData":[OSD([subQ2])],"isStart":false}),subQ1,subQ0]})])]})});}
            var Q92;
            {var subQ0=sQuery(id+"F23.wireOp",EDGE,"E21");var subQ1=sQuery(id+"F23.wireOp",EDGE,"E20");var subQ2=sQuery(id+"F21.wireOp",EDGE,"E19");Q92=makeQuery(id+"F24.boolean.opBoolean","COPY",EDGE,{"derivedFrom":makeQuery(id+"F24.opExtrude","SWEPT_EDGE",EDGE,{"disambiguationData":[OSD([subQ2,subQ1,subQ0]),TDD([makeQuery(id+"F23.imprint","INTERSECT",VERTEX,{"disambiguationData":[OD(1.0)],"derivedFrom":[makeQuery(id+"F22.opExtrude","CAP_EDGE",EDGE,{"disambiguationData":[OSD([subQ2])],"isStart":false}),subQ1,subQ0]})])]})});}
            var Q93;
            Q93=makeQuery(id+"F24.boolean.opBoolean","COPY",EDGE,{"derivedFrom":makeQuery(id+"F24.opExtrude","CAP_EDGE",EDGE,{"disambiguationData":[OSD([sQuery(id+"F23.wireOp",EDGE,"E20")])],"isStart":true})});
            var Q94;
            Q94=makeQuery(id+"F24.boolean.opBoolean","COPY",EDGE,{"derivedFrom":makeQuery(id+"F24.opExtrude","CAP_EDGE",EDGE,{"disambiguationData":[OSD([sQuery(id+"F23.wireOp",EDGE,"E20")])],"isStart":false})});
            var Q95;
            Q95=makeQuery(id+"F24.boolean.opBoolean","SPLIT",EDGE,{"disambiguationData":[OD(0.0)],"derivedFrom":makeQuery(id+"F22.opExtrude","CAP_EDGE",EDGE,{"disambiguationData":[OSD([sQuery(id+"F21.wireOp",EDGE,"E19")])],"isStart":false})});
            var Q96;
            Q96=makeQuery(id+"F24.boolean.opBoolean","SPLIT",EDGE,{"disambiguationData":[OD(1.0)],"derivedFrom":makeQuery(id+"F22.opExtrude","CAP_EDGE",EDGE,{"disambiguationData":[OSD([sQuery(id+"F21.wireOp",EDGE,"E19")])],"isStart":false})});
            var Q97;
            Q97=makeQuery(id+"F29.opExtrude","CAP_EDGE",EDGE,{"disambiguationData":[OSD([sQuery(id+"F28.wireOp",EDGE,"E24")])],"isStart":true});
            var Q98;
            {var subQ0=sQuery(id+"F30.wireOp",EDGE,"E27");var subQ1=sQuery(id+"F30.wireOp",EDGE,"E26");var subQ2=sQuery(id+"F28.wireOp",EDGE,"E25");Q98=makeQuery(id+"F31.boolean.opBoolean","COPY",EDGE,{"derivedFrom":makeQuery(id+"F31.opExtrude","SWEPT_EDGE",EDGE,{"disambiguationData":[OSD([subQ2,subQ1,subQ0]),TDD([makeQuery(id+"F30.imprint","INTERSECT",VERTEX,{"disambiguationData":[OD(0.0)],"derivedFrom":[makeQuery(id+"F29.opExtrude","CAP_EDGE",EDGE,{"disambiguationData":[OSD([subQ2])],"isStart":false}),subQ1,subQ0]})])]})});}
            var Q99;
            {var subQ0=sQuery(id+"F30.wireOp",EDGE,"E27");var subQ1=sQuery(id+"F30.wireOp",EDGE,"E26");var subQ2=sQuery(id+"F28.wireOp",EDGE,"E25");Q99=makeQuery(id+"F31.boolean.opBoolean","COPY",EDGE,{"derivedFrom":makeQuery(id+"F31.opExtrude","SWEPT_EDGE",EDGE,{"disambiguationData":[OSD([subQ2,subQ1,subQ0]),TDD([makeQuery(id+"F30.imprint","INTERSECT",VERTEX,{"disambiguationData":[OD(1.0)],"derivedFrom":[makeQuery(id+"F29.opExtrude","CAP_EDGE",EDGE,{"disambiguationData":[OSD([subQ2])],"isStart":false}),subQ1,subQ0]})])]})});}
            var Q100;
            Q100=makeQuery(id+"F31.boolean.opBoolean","COPY",EDGE,{"derivedFrom":makeQuery(id+"F31.opExtrude","CAP_EDGE",EDGE,{"disambiguationData":[OSD([sQuery(id+"F30.wireOp",EDGE,"E26")])],"isStart":true})});
            var Q101;
            Q101=makeQuery(id+"F31.boolean.opBoolean","COPY",EDGE,{"derivedFrom":makeQuery(id+"F31.opExtrude","CAP_EDGE",EDGE,{"disambiguationData":[OSD([sQuery(id+"F30.wireOp",EDGE,"E26")])],"isStart":false})});
            var Q102;
            Q102=makeQuery(id+"F31.boolean.opBoolean","SPLIT",EDGE,{"disambiguationData":[OD(0.0)],"derivedFrom":makeQuery(id+"F29.opExtrude","CAP_EDGE",EDGE,{"disambiguationData":[OSD([sQuery(id+"F28.wireOp",EDGE,"E25")])],"isStart":false})});
            var Q103;
            Q103=makeQuery(id+"F31.boolean.opBoolean","SPLIT",EDGE,{"disambiguationData":[OD(1.0)],"derivedFrom":makeQuery(id+"F29.opExtrude","CAP_EDGE",EDGE,{"disambiguationData":[OSD([sQuery(id+"F28.wireOp",EDGE,"E25")])],"isStart":false})});
            var Q104;
            Q104=makeQuery(id+"F3.boolean.opBoolean","COPY",FACE,{"derivedFrom":makeQuery(id+"F3.opExtrude","SWEPT_FACE",FACE,{"disambiguationData":[OSD([sQuery(id+"F2.wireOp",EDGE,"E2")])]})});
            var Q105;
            Q105=makeQuery(id+"F36.opExtrude","CAP_EDGE",EDGE,{"disambiguationData":[OSD([sQuery(id+"F35.wireOp",EDGE,"E30")])],"isStart":true});
            var Q106;
            {var subQ0=sQuery(id+"F37.wireOp",EDGE,"E33");var subQ1=sQuery(id+"F37.wireOp",EDGE,"E32");var subQ2=sQuery(id+"F35.wireOp",EDGE,"E31");Q106=makeQuery(id+"F38.boolean.opBoolean","COPY",EDGE,{"derivedFrom":makeQuery(id+"F38.opExtrude","SWEPT_EDGE",EDGE,{"disambiguationData":[OSD([subQ2,subQ1,subQ0]),TDD([makeQuery(id+"F37.imprint","INTERSECT",VERTEX,{"disambiguationData":[OD(0.0)],"derivedFrom":[makeQuery(id+"F36.opExtrude","CAP_EDGE",EDGE,{"disambiguationData":[OSD([subQ2])],"isStart":false}),subQ1,subQ0]})])]})});}
            var Q107;
            {var subQ0=sQuery(id+"F37.wireOp",EDGE,"E33");var subQ1=sQuery(id+"F37.wireOp",EDGE,"E32");var subQ2=sQuery(id+"F35.wireOp",EDGE,"E31");Q107=makeQuery(id+"F38.boolean.opBoolean","COPY",EDGE,{"derivedFrom":makeQuery(id+"F38.opExtrude","SWEPT_EDGE",EDGE,{"disambiguationData":[OSD([subQ2,subQ1,subQ0]),TDD([makeQuery(id+"F37.imprint","INTERSECT",VERTEX,{"disambiguationData":[OD(1.0)],"derivedFrom":[makeQuery(id+"F36.opExtrude","CAP_EDGE",EDGE,{"disambiguationData":[OSD([subQ2])],"isStart":false}),subQ1,subQ0]})])]})});}
            var Q108;
            Q108=makeQuery(id+"F38.boolean.opBoolean","COPY",EDGE,{"derivedFrom":makeQuery(id+"F38.opExtrude","CAP_EDGE",EDGE,{"disambiguationData":[OSD([sQuery(id+"F37.wireOp",EDGE,"E32")])],"isStart":true})});
            var Q109;
            Q109=makeQuery(id+"F38.boolean.opBoolean","COPY",EDGE,{"derivedFrom":makeQuery(id+"F38.opExtrude","CAP_EDGE",EDGE,{"disambiguationData":[OSD([sQuery(id+"F37.wireOp",EDGE,"E32")])],"isStart":false})});
            var Q110;
            Q110=makeQuery(id+"F38.boolean.opBoolean","SPLIT",EDGE,{"disambiguationData":[OD(0.0)],"derivedFrom":makeQuery(id+"F36.opExtrude","CAP_EDGE",EDGE,{"disambiguationData":[OSD([sQuery(id+"F35.wireOp",EDGE,"E31")])],"isStart":false})});
            var Q111;
            Q111=makeQuery(id+"F38.boolean.opBoolean","SPLIT",EDGE,{"disambiguationData":[OD(1.0)],"derivedFrom":makeQuery(id+"F36.opExtrude","CAP_EDGE",EDGE,{"disambiguationData":[OSD([sQuery(id+"F35.wireOp",EDGE,"E31")])],"isStart":false})});
            var Q112;
            Q112=makeQuery(id+"F3.boolean.opBoolean","COPY",EDGE,{"derivedFrom":makeQuery(id+"F3.opExtrude","CAP_EDGE",EDGE,{"disambiguationData":[OSD([sQuery(id+"F2.wireOp",EDGE,"E5.MirrorC")])],"isStart":true})});
            var Q113;
            Q113=makeQuery(id+"F3.boolean.opBoolean","COPY",EDGE,{"derivedFrom":makeQuery(id+"F3.opExtrude","CAP_EDGE",EDGE,{"disambiguationData":[OSD([sQuery(id+"F2.wireOp",EDGE,"E6.MirrorC")])],"isStart":true})});
            var Q114;
            Q114=makeQuery(id+"F3.boolean.opBoolean","COPY",EDGE,{"derivedFrom":makeQuery(id+"F3.opExtrude","CAP_EDGE",EDGE,{"disambiguationData":[OSD([sQuery(id+"F2.wireOp",EDGE,"E3")])],"isStart":true})});
            var Q115;
            Q115=makeQuery(id+"F17.boolean.opBoolean","COPY",EDGE,{"derivedFrom":makeQuery(id+"F17.opExtrude","CAP_EDGE",EDGE,{"disambiguationData":[OSD([sQuery(id+"F16.wireOp",EDGE,"E15")])],"isStart":false})});
            var Q116;
            Q116=makeQuery(id+"F3.boolean.opBoolean","COPY",EDGE,{"derivedFrom":makeQuery(id+"F3.opExtrude","CAP_EDGE",EDGE,{"disambiguationData":[OSD([sQuery(id+"F2.wireOp",EDGE,"E2")])],"isStart":true})});
            var Q117;
            Q117=makeQuery(id+"F3.boolean.opBoolean","COPY",EDGE,{"derivedFrom":makeQuery(id+"F3.opExtrude","CAP_EDGE",EDGE,{"disambiguationData":[OSD([sQuery(id+"F2.wireOp",EDGE,"E4")])],"isStart":true})});
            var Q118;
            Q118=makeQuery(id+"F20.opExtrude","CAP_EDGE",EDGE,{"disambiguationData":[OSD([sQuery(id+"F19.wireOp",EDGE,"E16")])],"isStart":false});
            var Q119;
            Q119=makeQuery(id+"F22.boolean.opBoolean","SPLIT",EDGE,{"disambiguationData":[OD(0.0)],"derivedFrom":makeQuery(id+"F22.opExtrude","CAP_EDGE",EDGE,{"disambiguationData":[OSD([sQuery(id+"F21.wireOp",EDGE,"E19")])],"isStart":true})});
            var Q120;
            Q120=makeQuery(id+"F22.boolean.opBoolean","SPLIT",EDGE,{"disambiguationData":[OD(1.0)],"derivedFrom":makeQuery(id+"F22.opExtrude","CAP_EDGE",EDGE,{"disambiguationData":[OSD([sQuery(id+"F21.wireOp",EDGE,"E19")])],"isStart":true})});
            var Q121;
            Q121=makeQuery(id+"F24.boolean.opBoolean","COPY",EDGE,{"derivedFrom":makeQuery(id+"F24.opExtrude","CAP_EDGE",EDGE,{"disambiguationData":[OSD([sQuery(id+"F23.wireOp",EDGE,"E21")])],"isStart":false})});
            var Q122;
            Q122=makeQuery(id+"F27.opExtrude","CAP_EDGE",EDGE,{"disambiguationData":[OSD([sQuery(id+"F26.wireOp",EDGE,"E22")])],"isStart":false});
            var Q123;
            Q123=makeQuery(id+"F29.boolean.opBoolean","SPLIT",EDGE,{"disambiguationData":[OD(0.0)],"derivedFrom":makeQuery(id+"F29.opExtrude","CAP_EDGE",EDGE,{"disambiguationData":[OSD([sQuery(id+"F28.wireOp",EDGE,"E25")])],"isStart":true})});
            var Q124;
            Q124=makeQuery(id+"F29.boolean.opBoolean","SPLIT",EDGE,{"disambiguationData":[OD(1.0)],"derivedFrom":makeQuery(id+"F29.opExtrude","CAP_EDGE",EDGE,{"disambiguationData":[OSD([sQuery(id+"F28.wireOp",EDGE,"E25")])],"isStart":true})});
            var Q125;
            Q125=makeQuery(id+"F31.boolean.opBoolean","COPY",EDGE,{"derivedFrom":makeQuery(id+"F31.opExtrude","CAP_EDGE",EDGE,{"disambiguationData":[OSD([sQuery(id+"F30.wireOp",EDGE,"E27")])],"isStart":false})});
            var Q126;
            Q126=makeQuery(id+"F34.opExtrude","CAP_EDGE",EDGE,{"disambiguationData":[OSD([sQuery(id+"F33.wireOp",EDGE,"E28")])],"isStart":false});
            var Q127;
            Q127=makeQuery(id+"F36.boolean.opBoolean","SPLIT",EDGE,{"disambiguationData":[OD(0.0)],"derivedFrom":makeQuery(id+"F36.opExtrude","CAP_EDGE",EDGE,{"disambiguationData":[OSD([sQuery(id+"F35.wireOp",EDGE,"E31")])],"isStart":true})});
            var Q128;
            Q128=makeQuery(id+"F36.boolean.opBoolean","SPLIT",EDGE,{"disambiguationData":[OD(1.0)],"derivedFrom":makeQuery(id+"F36.opExtrude","CAP_EDGE",EDGE,{"disambiguationData":[OSD([sQuery(id+"F35.wireOp",EDGE,"E31")])],"isStart":true})});
            var Q129;
            Q129=makeQuery(id+"F38.boolean.opBoolean","COPY",EDGE,{"derivedFrom":makeQuery(id+"F38.opExtrude","CAP_EDGE",EDGE,{"disambiguationData":[OSD([sQuery(id+"F37.wireOp",EDGE,"E33")])],"isStart":false})});
            fillet(context, id + "F39", {"entities" : qUnion([Q0, Q1, Q2, Q3, Q4, Q5, Q6, Q7, Q8, Q9, Q10, Q11, Q12, Q13, Q14, Q15, Q16, Q17, Q18, Q19, Q20, Q21, Q22, Q23, Q24, Q25, Q26, Q27, Q28, Q29, Q30, Q31, Q32, Q33, Q34, Q35, Q36, Q37, Q38, Q39, Q40, Q41, Q42, Q43, Q44, Q45, Q46, Q47, Q48, Q49, Q50, Q51, Q52, Q53, Q54, Q55, Q56, Q57, Q58, Q59, Q60, Q61, Q62, Q63, Q64, Q65, Q66, Q67, Q68, Q69, Q70, Q71, Q72, Q73, Q74, Q75, Q76, Q77, Q78, Q79, Q80, Q81, Q82, Q83, Q84, Q85, Q86, Q87, Q88, Q89, Q90, Q91, Q92, Q93, Q94, Q95, Q96, Q97, Q98, Q99, Q100, Q101, Q102, Q103, Q104, Q105, Q106, Q107, Q108, Q109, Q110, Q111, Q112, Q113, Q114, Q115, Q116, Q117, Q118, Q119, Q120, Q121, Q122, Q123, Q124, Q125, Q126, Q127, Q128, Q129]), "radius" : 0.25 * mm, "tangentPropagation" : true, "allowEdgeOverflow" : false});
        }
    });
